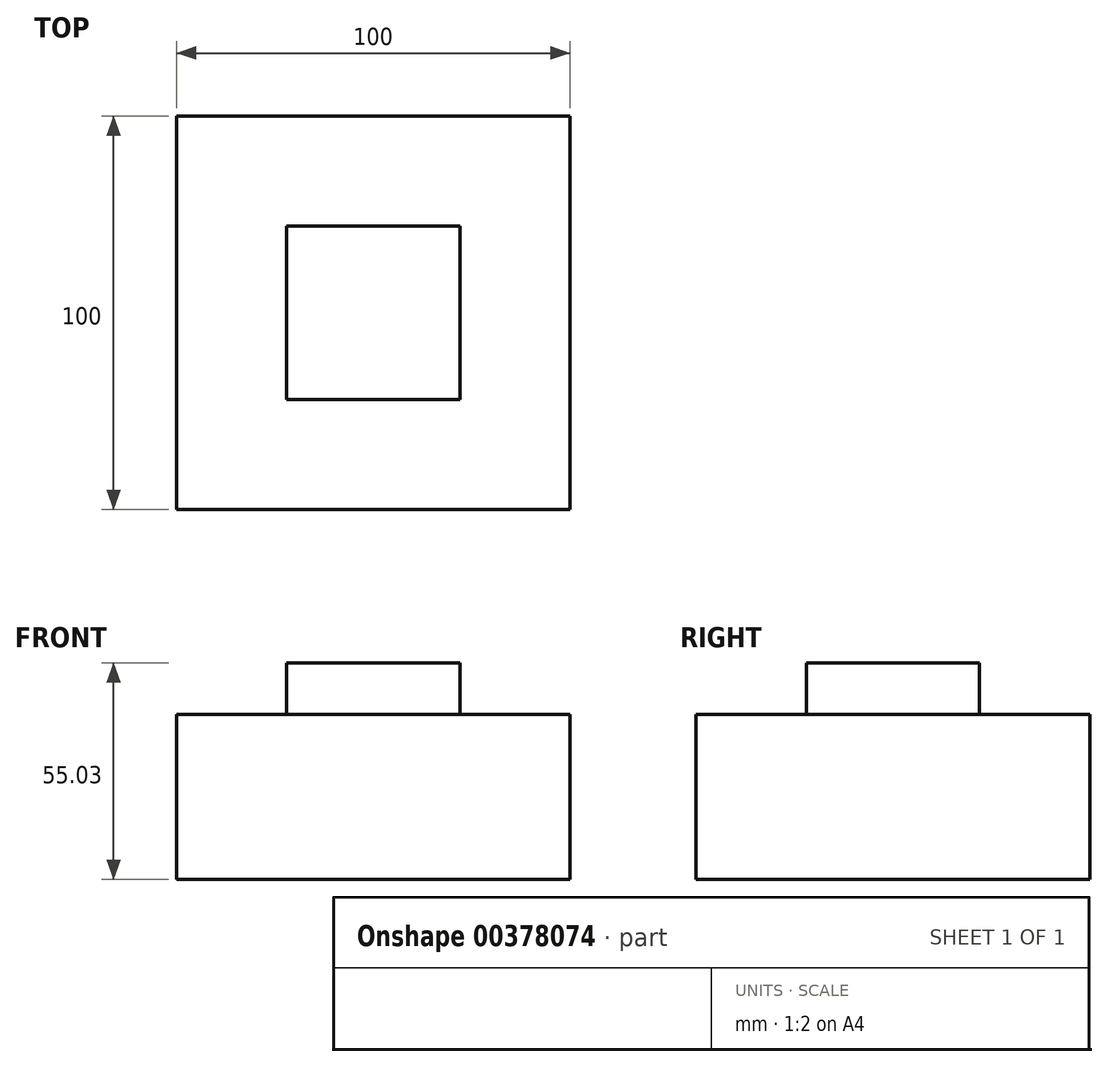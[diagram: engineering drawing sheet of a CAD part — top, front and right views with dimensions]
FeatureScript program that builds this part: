
annotation { "Feature Type Name" : "Feature", "Feature Type Description" : "" }
export const myFeature = defineFeature(function(context is Context, id is Id, definition is map)
    precondition{}
    {
        {
            var Q0;
            Q0=qCreatedBy(makeId("Front.planeOp"),FACE);
            var sketch = newSketch(context, id + "F0", { "sketchPlane" : qUnion([Q0])});
            skLineSegment(sketch, "E0", {"start": v(0, 13.05) * mm, "end": v(22, 13.05) * mm});
            skLineSegment(sketch, "E1", {"start": v(0, -41.98) * mm, "end": v(50, -41.98) * mm});
            skLineSegment(sketch, "E2", {"start": v(0, 54.54) * mm, "end": v(0, -57.96) * mm, "construction": true});
            skLineSegment(sketch, "E3", {"start": v(22, 13.05) * mm, "end": v(22, 0) * mm});
            skLineSegment(sketch, "E4", {"start": v(50, -41.98) * mm, "end": v(50, 0) * mm});
            skLineSegment(sketch, "E5", {"start": v(50, 0) * mm, "end": v(22, 0) * mm});
            skLineSegment(sketch, "E6.MirrorCS", {"start": v(0, 13.05) * mm, "end": v(-22, 13.05) * mm});
            skLineSegment(sketch, "E7.MirrorCS", {"start": v(-22, 13.05) * mm, "end": v(-22, 0) * mm});
            skLineSegment(sketch, "E8.MirrorCS", {"start": v(-50, 0) * mm, "end": v(-22, 0) * mm});
            skLineSegment(sketch, "E9.MirrorCS", {"start": v(-50, -41.98) * mm, "end": v(-50, 0) * mm});
            skLineSegment(sketch, "E10.MirrorCS", {"start": v(0, -41.98) * mm, "end": v(-50, -41.98) * mm});
            skLineSegment(sketch, "E11", {"start": v(-22, 0) * mm, "end": v(22, 0) * mm});
            skSolve(sketch);
        }
        {
            var Q0;
            Q0=makeQuery(id+"F0.imprint","IMPRINT",FACE,{"disambiguationData":[TD([[makeQuery(id+"F0.imprint","IMPRINT",EDGE,{"derivedFrom":sQuery(id+"F0.wireOp",EDGE,"E0")}),-1.0]])]});
            extrude(context, id + "F1", {"entities" : qUnion([Q0]), "depth" : 44 * mm});
        }
        {
            var Q0;
            Q0=makeQuery(id+"F0.imprint","IMPRINT",FACE,{"disambiguationData":[TD([[makeQuery(id+"F0.imprint","IMPRINT",EDGE,{"derivedFrom":sQuery(id+"F0.wireOp",EDGE,"E1")}),1.0]])]});
            extrude(context, id + "F2", {"entities" : qUnion([Q0]), "operationType" : NewBodyOperationType.ADD, "depth" : 72 * mm});
        }
        {
            var Q0;
            Q0=makeQuery(id+"F0.imprint","IMPRINT",FACE,{"disambiguationData":[TD([[makeQuery(id+"F0.imprint","IMPRINT",EDGE,{"derivedFrom":sQuery(id+"F0.wireOp",EDGE,"E1")}),1.0]])]});
            extrude(context, id + "F3", {"entities" : qUnion([Q0]), "operationType" : NewBodyOperationType.ADD, "oppositeDirection" : true, "depth" : 28 * mm});
        }
    });
